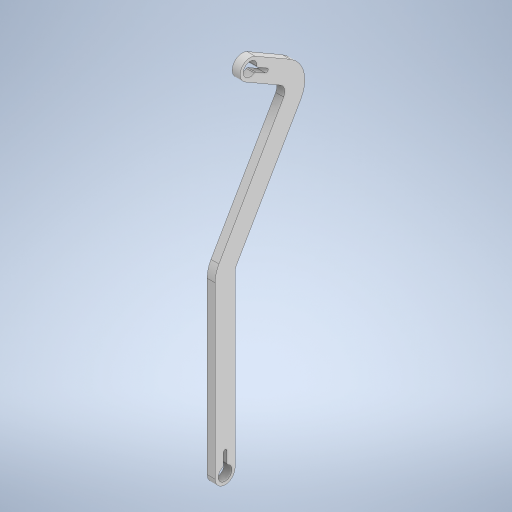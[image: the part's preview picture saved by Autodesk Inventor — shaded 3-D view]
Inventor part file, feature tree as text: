
AUTODESK INVENTOR PART (.ipt)
format: ipt  version: 2024 (Build 280153000, 153)  size: 334,336 bytes
history: native  units: mm
features: sketch x3, extrude x3, projected_geometry x2, thicken_offset x1, hole x1, fillet x1, other x1
ambient origin geometry x8: Origin, YZ Plane, XZ Plane, XY Plane, X Axis, Y Axis, Z Axis, Center Point
bodies: Solid1 (feature_tree)
feature tree (12):
  sketch  "Sketch1"  dims[d0=270.0mm d4=20.0mm]
  thicken_offset  "Thicken1"
  sketch  "Sketch4"  dims[d5=20.0mm d9=6.35mm d10=0.0mm]
  extrude  "Extrusion2"  Depth=20.0mm
  hole  "Hole4"  [1 undecoded]
  extrude  "Extrusion3"  Depth=15.0mm
  fillet  "Fillet4"  Radius=17.0mm
  other  "Srf1"
  projected_geometry  "Projected Loop1"
  sketch  "Sketch5"  dims[d14=16.0mm d60=20.0mm d65=17.0mm d66=160.0mm d68=11.5mm d72=10.0mm d73=0.0mm d74=11.05mm d75=10.0mm d76=4.0mm d77=2.0mm d78=90.0deg d79=8.0mm d80=20.594885mm d82=150.0deg d83=140.0mm d84=15.0mm d86=3.0mm d87=15.0mm d90=0.0mm d91=0.0mm d92=1.0mm d93=15.0mm]
  projected_geometry  "Projected Loop2"
  extrude  "ExtrusionSrf1"  Depth=15.0mm
note: 1 required parameter value undecoded (feature->parameter linkage not recoverable at this tier; creation-order binding heuristic only, values carry confidence <= 0.55)
